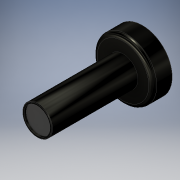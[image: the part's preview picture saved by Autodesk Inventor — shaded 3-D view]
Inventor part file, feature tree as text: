
AUTODESK INVENTOR PART (.ipt)
format: ipt  version: 2019 (Build 230136000, 136)  size: 141,824 bytes
history: native  units: mm
features: extrude x3, sketch x3, chamfer x2, fillet x1
ambient origin geometry x8: Origin, YZ Plane, XZ Plane, XY Plane, X Axis, Y Axis, Z Axis, Center Point
bodies: Solid1 (feature_tree)
feature tree (9):
  extrude  "Extrusion1"  Depth=10.0mm TaperAngle=0.0deg
  extrude  "Extrusion2"  Depth=43.2mm TaperAngle=0.0deg
  extrude  "Extrusion3"  Depth=1.0mm TaperAngle=0.0deg
  fillet  "Fillet1"  Radius=2.0mm
  chamfer  "Chamfer1"  Distance=2.0mm Angle=45.0deg
  chamfer  "Chamfer2"  Distance=2.0mm Angle=45.0deg
  sketch  "Sketch1"  dims[d0=30.0mm d1=10.0mm d2=0.0mm]
  sketch  "Sketch2"  dims[d3=15.0mm d4=43.2mm d5=0.0mm]
  sketch  "Sketch3"  dims[d6=1.0mm d7=1.0mm d8=0.0mm d9=2.0mm d10=0.25mm d11=2.0mm d12=45.0deg d13=0.25mm d14=2.0mm d15=45.0deg]
